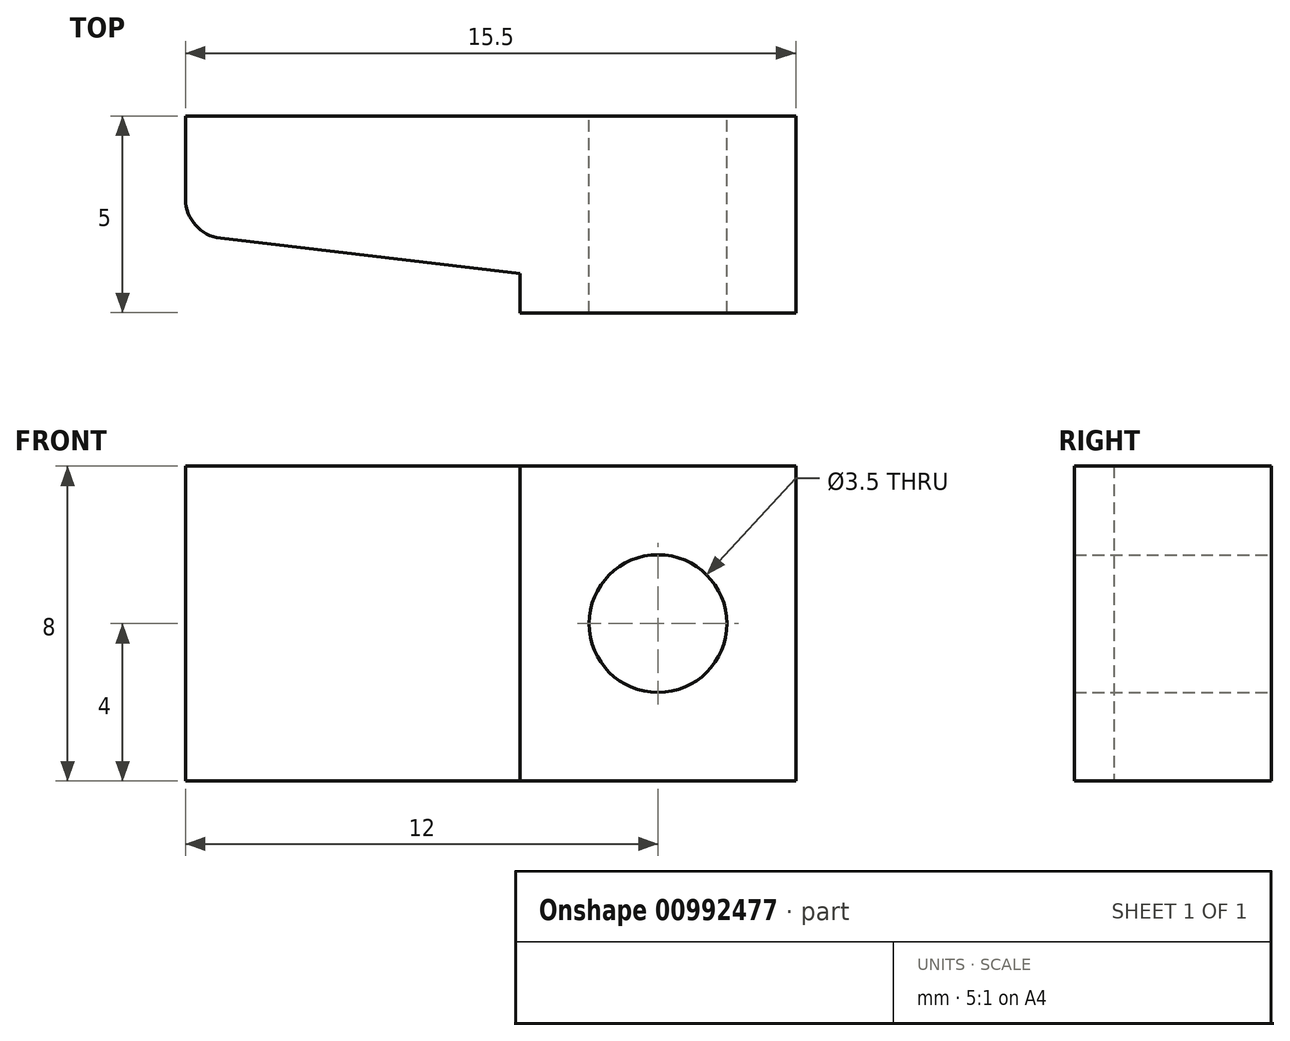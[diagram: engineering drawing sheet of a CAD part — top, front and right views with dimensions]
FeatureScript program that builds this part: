
annotation { "Feature Type Name" : "Feature", "Feature Type Description" : "" }
export const myFeature = defineFeature(function(context is Context, id is Id, definition is map)
    precondition{}
    {
        {
            var Q0;
            Q0=qCreatedBy(makeId("Top.planeOp"),FACE);
            var sketch = newSketch(context, id + "F0", { "sketchPlane" : qUnion([Q0])});
            skLineSegment(sketch, "E0.bottom", {"start": v(4.05, 1.83) * mm, "end": v(-11.45, 1.83) * mm});
            skLineSegment(sketch, "E0.top", {"start": v(4.05, -3.17) * mm, "end": v(-2.95, -3.17) * mm});
            skLineSegment(sketch, "E0.left", {"start": v(4.05, 1.83) * mm, "end": v(4.05, -3.17) * mm});
            skLineSegment(sketch, "E0.right", {"start": v(-11.45, 1.83) * mm, "end": v(-11.45, -1.17) * mm});
            skLineSegment(sketch, "E1", {"start": v(-11.45, -1.17) * mm, "end": v(-2.95, -2.17) * mm});
            skLineSegment(sketch, "E2", {"start": v(-2.95, -2.17) * mm, "end": v(-2.95, -3.17) * mm});
            skSolve(sketch);
        }
        {
            var Q0;
            Q0=makeQuery(id+"F0.imprint","IMPRINT",FACE,{"disambiguationData":[TD([[makeQuery(id+"F0.imprint","IMPRINT",EDGE,{"derivedFrom":sQuery(id+"F0.wireOp",EDGE,"E0.bottom")}),1.0]])]});
            extrude(context, id + "F1", {"entities" : qUnion([Q0]), "depth" : 8 * mm, "offsetDistance" : 25 * mm});
        }
        {
            var Q0;
            Q0=makeQuery(id+"F1.opExtrude","SWEPT_FACE",FACE,{"disambiguationData":[OSD([sQuery(id+"F0.wireOp",EDGE,"E0.bottom")])]});
            var sketch = newSketch(context, id + "F2", { "sketchPlane" : qUnion([Q0])});
            skCircle(sketch, "E3", {"center": v(-0.55, 4) * mm, "radius": 1.75 * mm});
            skSolve(sketch);
        }
        {
            var Q0;
            Q0=makeQuery(id+"F2.imprint","IMPRINT",FACE,{"disambiguationData":[TD([[makeQuery(id+"F2.imprint","IMPRINT",EDGE,{"derivedFrom":sQuery(id+"F2.wireOp",EDGE,"E3")}),1.0]])]});
            var Q1;
            Q1=makeQuery(id+"F1.opExtrude","SWEPT_FACE",FACE,{"disambiguationData":[OSD([sQuery(id+"F0.wireOp",EDGE,"E0.top")])]});
            extrude(context, id + "F3", {"entities" : qUnion([Q0]), "operationType" : NewBodyOperationType.REMOVE, "endBound" : BoundingType.UP_TO_SURFACE, "oppositeDirection" : true, "depth" : 25 * mm, "endBoundEntityFace" : qUnion([Q1]), "offsetDistance" : 25 * mm});
        }
        {
            var Q0;
            Q0=makeQuery(id+"F1.opExtrude","SWEPT_EDGE",EDGE,{"disambiguationData":[OSD([sQuery(id+"F0.wireOp",EDGE,"E0.right"),sQuery(id+"F0.wireOp",EDGE,"E1")])]});
            fillet(context, id + "F4", {"entities" : qUnion([Q0]), "radius" : 1 * mm, "tangentPropagation" : true, "allowEdgeOverflow" : false});
        }
    });
